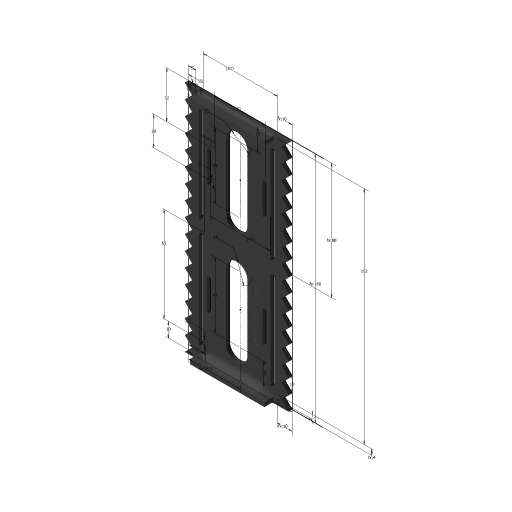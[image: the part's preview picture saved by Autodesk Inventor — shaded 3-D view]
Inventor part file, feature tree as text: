
AUTODESK INVENTOR PART (.ipt)
format: ipt  version: 2023 (Build 270158000, 158)  size: 605,696 bytes
history: native  units: mm
features: extrude x6, sketch x2, fillet x2
ambient origin geometry x8: Origin, YZ Plane, XZ Plane, XY Plane, X Axis, Y Axis, Z Axis, Center Point
bodies: Solid1 (feature_tree)
feature tree (10):
  sketch  "Sketch1"  dims[d0=71.0mm d1=160.0mm]
  extrude  "Extrusion1"  Depth=160.0mm
  extrude  "Extrusion2"  Depth=160.0mm
  fillet  "Fillet1"  Radius=160.0mm
  extrude  "Extrusion3"  Depth=160.0mm
  extrude  "Extrusion4"  Depth=160.0mm
  fillet  "Fillet2"  Radius=10.0mm
  extrude  "Extrusion5"  Depth=160.0mm
  extrude  "Extrusion6"  Depth=160.0mm
  sketch  "Sketch2"  dims[d2=45.0deg d3=5.0mm d4=160.0mm d6=10.0mm d7=10.0mm d9=10.0mm d11=35.5mm d12=10.0mm d13=10.0mm d14=3.0mm d15=10.0mm d16=3.0mm d17=152.0mm d19=4.0mm d20=3.2mm d21=11.0mm d22=10.0mm d24=51.0mm d25=3.0mm d26=4.0mm d27=32.0mm d28=20.0mm d29=35.0mm d30=41.0mm d31=2.5mm d32=0.0mm d33=9.0mm d34=0.0mm d35=3.0mm d36=45.0mm d37=15.0mm d38=15.0mm d39=45.0mm d40=15.0mm d41=15.0mm d42=0.0mm d43=0.0mm d44=65.0mm d45=80.0mm d46=0.0mm d47=0.0mm d48=20.0mm d50=10.0mm d51=10.0mm d53=10.0mm d55=0.0mm d56=0.0mm d57=5.0mm d58=2.0mm d59=5.0mm d60=8.0mm d61=0.0mm d62=0.0mm d63=5.0mm d64=2.0mm d65=5.0mm d66=8.0mm d67=1.0mm d68=0.0mm d69=0.0mm d70=0.0mm]
